# Revit family: BOS-LineaOutside-SvdW-STW_Familie
name_source: partatom
category: Türen
revit_build: Autodesk Revit 2017 (Build: 20160225_1515(x64)
units: mm (PartAtom-declared; Revit-internal decimal feet)

## family parameters
Basisbauteil = Wand
Beim Laden mit Abzugskörper schneiden = Nein
Gemeinsam genutzt = Nein
Immer vertikal = Ja
Raumberechnungspunkt = Ja

## types (5) — shared parameters
BE max. = 100 mm  [stored 0.328084 ft]
Bauelement = BOS Stahlzarge
Beschreibung = Schiebetürzarge für vor der Wand laufende Schiebetüren (LineaOutside) für Ständerwerk
Einfügepunkt = 30 mm  [stored 0.0984252 ft]
Endkappenstärke = 3 mm  [stored 0.00984252 ft]
Funktion = Innen
GT max. = 650 mm  [stored 2.13255 ft]
Glastürblattstärke = 8 mm  [stored 0.0262467 ft]
Hersteller = BOS GmbH Best Of Steel, Lütkenfelde 4, D-48282 Emsdetten
Holztürblattstärke = 40 mm  [stored 0.131234 ft]
Info-Texte sichtbar = Ja
Information in English = Nein
LDB max. = 1686 mm  [stored 5.5315 ft]
LDB min. = 499 mm  [stored 1.63714 ft]
LDH max. = 2468 mm  [stored 8.09711 ft]
LDH min. = 1968 mm  [stored 6.45669 ft]
Laufkastenblechstärke = 2 mm  [stored 0.00656168 ft]
Laufkastenhöhe = 110 mm  [stored 0.360892 ft]
Laufschienenabstand = 55 mm  [stored 0.180446 ft]
Laufschienenachse = 39.5 mm
MW min. = 100 mm  [stored 0.328084 ft]
Material = grundiert, feuerverzinktes Feinblech nach DIN EN 10143
Material - Führungszapfen = <Nach Kategorie>
Material - Laufschiene = <Nach Kategorie>
Material - Türgriff = <Nach Kategorie>
Material - Zarge = <Nach Kategorie>
Putzwinkel max. = 28 mm  [stored 0.0918635 ft]
Putzwinkel min. = 10 mm  [stored 0.0328084 ft]
Technische Infos rund um die Stahlzarge = www.BestOfSteel.de/tools-downloads/technische-infos-rund-um-die-stahlzarge/
Türblatteinstand hinten = 40 mm  [stored 0.131234 ft]
Türblatteinstand vorne = 9 mm  [stored 0.0295276 ft]
URL = www.BestOfSteel.de/stahlzargen/zargen-fuer-schiebetueren/lineaoutside/lineaoutside/
Zargenblechstärke = 1.5 mm  [stored 0.00492126 ft]
zero-valued in all types: Breite, Dicke, Rohbaubreite, Rohbauhöhe

## per-type parameters (varying)
| type | ALU 100 BOS | ALU 150 BOS | ALU 80 BOS | Glastürblatt | Holztürblatt | Material - Türblatt | SvdW mit ALU 100 BOS Glas | SvdW mit ALU 100 BOS Holz | SvdW mit ALU 150 BOS Holz | SvdW mit ALU 80 BOS Glas | SvdW mit ALU 80 BOS Holz | Türblattachse |
| SvdW mit ALU 80 BOS Holz | Nein | Nein | Ja | Nein | Ja | <Nach Kategorie> | Nein | Nein | Nein | Nein | Ja | 42 mm  [stored 0.137795 ft] |
| SvdW mit ALU 100 BOS Glas | Ja | Nein | Nein | Ja | Nein | Glas | Ja | Nein | Nein | Nein | Nein | 39.5 mm |
| SvdW mit ALU 150 BOS Holz | Nein | Ja | Nein | Nein | Ja | <Nach Kategorie> | Nein | Nein | Ja | Nein | Nein | 42 mm  [stored 0.137795 ft] |
| SvdW mit ALU 100 BOS Holz | Ja | Nein | Nein | Nein | Ja | <Nach Kategorie> | Nein | Ja | Nein | Nein | Nein | 42 mm  [stored 0.137795 ft] |
| SvdW mit ALU 80 BOS Glas | Nein | Nein | Ja | Ja | Nein | <Nach Kategorie> | Nein | Nein | Nein | Ja | Nein | 39.5 mm |

note: column(s) folded — value = type name in every type: Modell

note: [stored X ft] marks values corroborated as IEEE doubles in the binary element streams (Revit-internal decimal feet)

## geometry (parser evidence)
native form markers: Extrusion x8
no freeform markers — native parametric forms only
